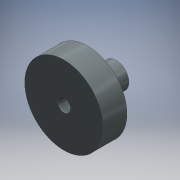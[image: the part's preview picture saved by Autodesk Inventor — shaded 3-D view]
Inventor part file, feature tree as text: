
AUTODESK INVENTOR PART (.ipt)
format: ipt  version: 2016 (Build 200138000, 138)  size: 107,520 bytes
history: native  units: mm
features: extrude x2, sketch x2
ambient origin geometry x8: Origin, YZ Plane, XZ Plane, XY Plane, X Axis, Y Axis, Z Axis, Center Point
bodies: Solid1 (feature_tree)
feature tree (4):
  extrude  "Extrusion1"  Depth=36.0mm
  extrude  "Extrusion2"  Depth=13.0mm
  sketch  "Sketch1"  dims[d0=6.1mm d1=36.0mm]
  sketch  "Sketch2"  dims[d2=11.0mm d3=0.0mm d4=11.75mm d5=13.0mm d6=0.0mm]
